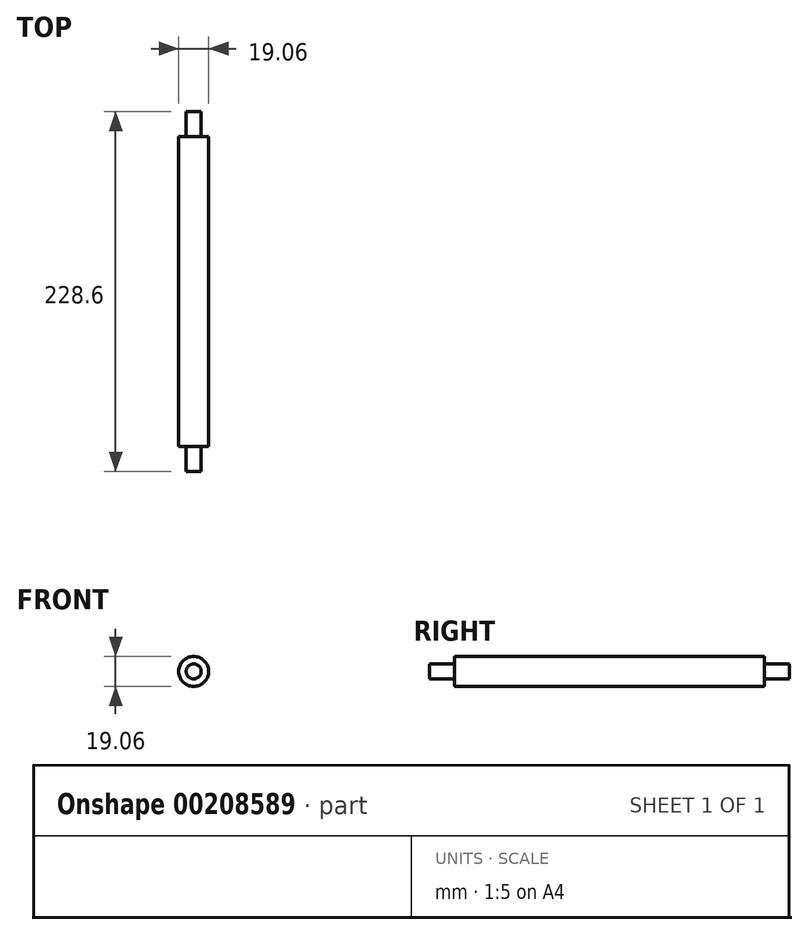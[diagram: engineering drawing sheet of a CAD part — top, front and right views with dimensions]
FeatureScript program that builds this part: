
annotation { "Feature Type Name" : "Feature", "Feature Type Description" : "" }
export const myFeature = defineFeature(function(context is Context, id is Id, definition is map)
    precondition{}
    {
        {
            var Q0;
            Q0=qCreatedBy(makeId("Right.planeOp"),FACE);
            var sketch = newSketch(context, id + "F0", { "sketchPlane" : qUnion([Q0])});
            skLineSegment(sketch, "E0", {"start": v(0, 0) * mm, "end": v(228.6, 0) * mm});
            skLineSegment(sketch, "E1", {"start": v(228.6, 0) * mm, "end": v(228.6, 4.76) * mm});
            skLineSegment(sketch, "E2", {"start": v(228.6, 4.76) * mm, "end": v(212.73, 4.76) * mm});
            skLineSegment(sketch, "E3", {"start": v(212.73, 4.76) * mm, "end": v(212.73, 9.53) * mm});
            skLineSegment(sketch, "E4", {"start": v(212.73, 9.53) * mm, "end": v(15.88, 9.53) * mm});
            skLineSegment(sketch, "E5", {"start": v(15.88, 9.52) * mm, "end": v(15.88, 4.76) * mm});
            skLineSegment(sketch, "E6", {"start": v(15.88, 4.76) * mm, "end": v(0, 4.76) * mm});
            skLineSegment(sketch, "E7", {"start": v(0, 4.76) * mm, "end": v(0, 0) * mm});
            skSolve(sketch);
        }
        {
            var Q0;
            Q0 = qSketchRegion(id + "F0", true);
            var Q1;
            Q1=sQuery(id+"F0.wireOp",EDGE,"E0");
            revolve(context, id + "F1", {"entities" : qUnion([Q0]), "axis" : qUnion([Q1]), "revolveType" : RevolveType.FULL});
        }
    });
